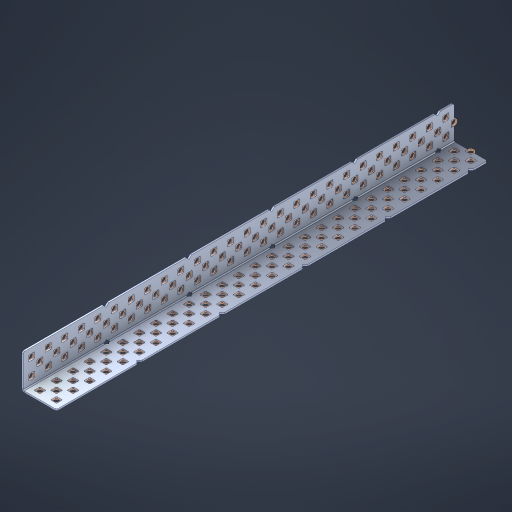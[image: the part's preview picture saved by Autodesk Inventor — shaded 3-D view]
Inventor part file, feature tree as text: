
AUTODESK INVENTOR PART (.ipt)
format: ipt  version: 2023 (Build 270158000, 158)  size: 1,872,384 bytes
history: native  units: in
note: dims shown in document units (in); Inventor stores cm internally (conversion verified against a paired STEP export)
features: other x162, extrude x154, sheet_metal_op x8, sketch x7, pattern_linear x2, mirror x1, chamfer x1
ambient origin geometry x8: Origin, YZ Plane, XZ Plane, XY Plane, X Axis, Y Axis, Z Axis, Center Point
bodies: Solid1 (feature_tree), Body (feature_tree)
feature tree (335):
  sheet_metal_op  "Flanges"
  sheet_metal_op  "Body Pattern"
  pattern_linear  "Center Pattern"  Spacing1=1.0in  [1 undecoded]
  other  "Arc Length"
  pattern_linear  "Notch Pattern"  Spacing1=0.1875in  [1 undecoded]
  other  "Diagonal Plane"
  mirror  "Everything Mirrored"
  chamfer  "End Chamfer"
  sketch  "Sketch1"  dims[d0=1.0in]
  other  "Plate1"
  sketch  "Sketch2"  dims[d1=13.0in]
  other  "Plate2"
  sheet_metal_op  "Bend1"
  sheet_metal_op  "Corner1"
  sketch  "Sketch8"  dims[d2=0.0469in]
  sketch  "Sketch9"  dims[d3=0.0469in]
  other  "Srf91"
  sheet_metal_op  "Body Pattern Sketch"
  other  "Srf92"
  sketch  "Sketch13"  dims[d4=0.0234in]
  sketch  "Sketch15"  dims[d5=0.0938in]
  sketch  "Sketch16"  dims[d6=0.0469in d7=1.0in d8=90.0deg d9=0.0312in d10=0.1875in d11=0.0469in d12=0.0469in d49=0.182in d50=0.02in d52=0.25in d53=0.0469in d54=0.0in d55=0.172in d56=1.0in d57=0.0in d60=10.2362in d62=0.5in d63=0.7874in d65=0.5in d85=0.1473in d86=0.1659in d89=0.0469in d90=0.0in d91=0.04in d92=0.0491in d95=2.5in d96=0.04in d97=0.25in d98=45.0deg d99=0.25in d106=0.182in d107=0.02in d108=0.5in d110=0.0469in d111=0.0in d112=0.172in d113=0.5in d114=0.0in d117=0.5in d123=0.25in d125=0.25in d126=0.0491in d127=0.1227in d128=0.08in d129=0.04in d130=2.5in]
  other  "Srf786"
  other  "Srf856"
  other  "Srf857"
  other  "Srf858"
  other  "Srf859"
  other  "Srf860"
  other  "Srf861"
  other  "Srf889"
  other  "Srf890"
  other  "Srf891"
  other  "Srf1275"
  other  "Srf1276"
  other  "Srf1278"
  other  "Srf1279"
  other  "Srf1280"
  other  "Srf1281"
  other  "Srf1282"
  other  "Srf1283"
  other  "Srf1277"
  other  "Srf1285"
  other  "Srf1286"
  other  "Srf1287"
  other  "Srf1383"
  other  "Srf1384"
  other  "Srf1385"
  other  "Srf1386"
  other  "Srf1387"
  other  "Srf1388"
  other  "Srf1389"
  other  "Srf1390"
  other  "Srf1391"
  other  "Srf1392"
  other  "Srf1393"
  other  "Srf1394"
  other  "Srf1395"
  other  "Srf1396"
  other  "Srf1397"
  other  "Srf1398"
  other  "Srf1399"
  other  "Srf1400"
  other  "Srf1401"
  other  "Srf1402"
  other  "Srf1403"
  other  "Srf1404"
  other  "Srf1405"
  other  "Srf1406"
  other  "Srf1407"
  other  "Srf1408"
  other  "Srf1409"
  other  "Srf1410"
  other  "Srf1411"
  other  "Srf1412"
  other  "Srf1413"
  other  "Srf1414"
  other  "Srf1415"
  other  "Srf1416"
  other  "Srf1417"
  other  "Srf1418"
  other  "Srf1419"
  other  "Srf1420"
  other  "Srf1421"
  other  "Srf1422"
  other  "Srf1423"
  other  "Srf1424"
  other  "Srf1425"
  other  "Srf1426"
  other  "Srf1445"
  other  "Srf1446"
  other  "Srf1447"
  other  "Srf1448"
  other  "Srf1449"
  other  "Srf1450"
  other  "Srf1451"
  other  "Srf1452"
  other  "Srf1453"
  other  "Srf1454"
  other  "Srf1455"
  other  "Srf1456"
  other  "Srf1457"
  other  "Srf1458"
  other  "Srf1459"
  other  "Srf1460"
  other  "Srf1461"
  other  "Srf1462"
  other  "Srf1463"
  other  "Srf1464"
  other  "Srf1465"
  other  "Srf1466"
  other  "Srf1475"
  other  "Srf1476"
  other  "Srf1477"
  other  "Srf1478"
  other  "Srf1479"
  other  "Srf1480"
  other  "Srf1481"
  other  "Srf1482"
  other  "Srf1483"
  other  "Srf1484"
  other  "Srf1485"
  other  "Srf1486"
  other  "Srf1487"
  other  "Srf1488"
  other  "Srf1489"
  other  "Srf1490"
  other  "Srf1491"
  other  "Srf1492"
  other  "Srf1493"
  other  "Srf1494"
  other  "Srf1495"
  other  "Srf1496"
  other  "Srf1497"
  other  "Srf1498"
  other  "Srf1499"
  other  "Srf1500"
  other  "Srf1501"
  other  "Srf1502"
  other  "Srf1503"
  other  "Srf1504"
  other  "Srf1505"
  other  "Srf1506"
  other  "Srf1507"
  other  "Srf1508"
  other  "Srf1509"
  other  "Srf1510"
  other  "Srf1511"
  other  "Srf1512"
  other  "Srf1513"
  other  "Srf1514"
  other  "Srf1515"
  other  "Srf1516"
  other  "Srf1517"
  other  "Srf1518"
  other  "Srf1537"
  other  "Srf1538"
  other  "Srf1539"
  other  "Srf1540"
  other  "Srf1541"
  other  "Srf1542"
  other  "Srf1543"
  other  "Srf1544"
  other  "Srf1545"
  other  "Srf1546"
  other  "Srf1547"
  other  "Srf1548"
  other  "Srf1549"
  other  "Srf1550"
  other  "Srf1551"
  other  "Srf1552"
  other  "Srf1553"
  other  "Srf1554"
  other  "Srf1555"
  other  "Srf1556"
  other  "Srf1557"
  other  "Srf1558"
  sheet_metal_op  "Body Stamp"
  sheet_metal_op  "Body Circle"
  other  "Center Stamp"
  other  "Center Circle"
  sheet_metal_op  "Notch"
  extrude  "ExtrusionSrf92"  Depth=0.0469in
  extrude  "ExtrusionSrf856"  Depth=0.0469in
  extrude  "ExtrusionSrf857"  Depth=0.182in
  extrude  "ExtrusionSrf858"  Depth=0.02in
  extrude  "ExtrusionSrf859"  Depth=0.25in
  extrude  "ExtrusionSrf860"  Depth=0.0469in
  extrude  "ExtrusionSrf861"  TaperAngle=0.0deg  [1 undecoded]
  extrude  "ExtrusionSrf889"  Depth=2.5in
  extrude  "ExtrusionSrf890"  Depth=1.0in TaperAngle=0.0deg
  extrude  "ExtrusionSrf891"  Depth=2.5in
  extrude  "ExtrusionSrf1275"  Depth=0.5in
  extrude  "ExtrusionSrf1276"  Depth=2.5in
  extrude  "ExtrusionSrf1277"  Depth=2.5in
  extrude  "ExtrusionSrf1278"  Depth=0.0469in
  extrude  "ExtrusionSrf1279"  Depth=2.5in TaperAngle=0.0deg
  extrude  "ExtrusionSrf1280"  Depth=2.5in
  extrude  "ExtrusionSrf1281"  Depth=0.25in TaperAngle=45.0deg
  extrude  "ExtrusionSrf1282"  Depth=0.25in
  extrude  "ExtrusionSrf1345"  Depth=0.182in
  extrude  "ExtrusionSrf1346"  Depth=0.02in
  extrude  "ExtrusionSrf1347"  Depth=0.5in
  extrude  "ExtrusionSrf1348"  Depth=0.0469in
  extrude  "ExtrusionSrf1383"  TaperAngle=0.0deg  [1 undecoded]
  extrude  "ExtrusionSrf1384"  Depth=2.5in
  extrude  "ExtrusionSrf1385"  Depth=0.5in TaperAngle=0.0deg
  extrude  "ExtrusionSrf1386"  Depth=0.5in
  extrude  "ExtrusionSrf1387"  Depth=0.25in
  extrude  "ExtrusionSrf1388"  Depth=0.25in
  extrude  "ExtrusionSrf1389"  Depth=2.5in
  extrude  "ExtrusionSrf1390"  Depth=2.5in
  extrude  "ExtrusionSrf1391"  Depth=2.5in
  extrude  "ExtrusionSrf1392"  Depth=2.5in
  extrude  "ExtrusionSrf1393"  Depth=2.5in
  extrude  "ExtrusionSrf1394"  [1 undecoded]
  extrude  "ExtrusionSrf1395"  [1 undecoded]
  extrude  "ExtrusionSrf1396"  [1 undecoded]
  extrude  "ExtrusionSrf1397"  [1 undecoded]
  extrude  "ExtrusionSrf1398"  [1 undecoded]
  extrude  "ExtrusionSrf1399"  [1 undecoded]
  extrude  "ExtrusionSrf1400"  [1 undecoded]
  extrude  "ExtrusionSrf1401"  [1 undecoded]
  extrude  "ExtrusionSrf1402"  [1 undecoded]
  extrude  "ExtrusionSrf1403"  [1 undecoded]
  extrude  "ExtrusionSrf1404"  [1 undecoded]
  extrude  "ExtrusionSrf1405"  [1 undecoded]
  extrude  "ExtrusionSrf1406"  [1 undecoded]
  extrude  "ExtrusionSrf1407"  [1 undecoded]
  extrude  "ExtrusionSrf1408"  [1 undecoded]
  extrude  "ExtrusionSrf1409"  [1 undecoded]
  extrude  "ExtrusionSrf1410"  [1 undecoded]
  extrude  "ExtrusionSrf1411"  [1 undecoded]
  extrude  "ExtrusionSrf1412"  [1 undecoded]
  extrude  "ExtrusionSrf1413"  [1 undecoded]
  extrude  "ExtrusionSrf1414"  [1 undecoded]
  extrude  "ExtrusionSrf1415"  [1 undecoded]
  extrude  "ExtrusionSrf1416"  [1 undecoded]
  extrude  "ExtrusionSrf1417"  [1 undecoded]
  extrude  "ExtrusionSrf1418"  [1 undecoded]
  extrude  "ExtrusionSrf1419"  [1 undecoded]
  extrude  "ExtrusionSrf1420"  [1 undecoded]
  extrude  "ExtrusionSrf1421"  [1 undecoded]
  extrude  "ExtrusionSrf1422"  [1 undecoded]
  extrude  "ExtrusionSrf1423"  [1 undecoded]
  extrude  "ExtrusionSrf1424"  [1 undecoded]
  extrude  "ExtrusionSrf1425"  [1 undecoded]
  extrude  "ExtrusionSrf1426"  [1 undecoded]
  extrude  "ExtrusionSrf1445"  [1 undecoded]
  extrude  "ExtrusionSrf1446"  [1 undecoded]
  extrude  "ExtrusionSrf1447"  [1 undecoded]
  extrude  "ExtrusionSrf1448"  [1 undecoded]
  extrude  "ExtrusionSrf1449"  [1 undecoded]
  extrude  "ExtrusionSrf1450"  [1 undecoded]
  extrude  "ExtrusionSrf1451"  [1 undecoded]
  extrude  "ExtrusionSrf1452"  [1 undecoded]
  extrude  "ExtrusionSrf1453"  [1 undecoded]
  extrude  "ExtrusionSrf1454"  [1 undecoded]
  extrude  "ExtrusionSrf1455"  [1 undecoded]
  extrude  "ExtrusionSrf1456"  [1 undecoded]
  extrude  "ExtrusionSrf1457"  [1 undecoded]
  extrude  "ExtrusionSrf1458"  [1 undecoded]
  extrude  "ExtrusionSrf1459"  [1 undecoded]
  extrude  "ExtrusionSrf1460"  [1 undecoded]
  extrude  "ExtrusionSrf1461"  [1 undecoded]
  extrude  "ExtrusionSrf1462"  [1 undecoded]
  extrude  "ExtrusionSrf1463"  [1 undecoded]
  extrude  "ExtrusionSrf1464"  [1 undecoded]
  extrude  "ExtrusionSrf1465"  [1 undecoded]
  extrude  "ExtrusionSrf1466"  [1 undecoded]
  extrude  "ExtrusionSrf1475"  [1 undecoded]
  extrude  "ExtrusionSrf1476"  [1 undecoded]
  extrude  "ExtrusionSrf1477"  [1 undecoded]
  extrude  "ExtrusionSrf1478"  [1 undecoded]
  extrude  "ExtrusionSrf1479"  [1 undecoded]
  extrude  "ExtrusionSrf1480"  [1 undecoded]
  extrude  "ExtrusionSrf1481"  [1 undecoded]
  extrude  "ExtrusionSrf1482"  [1 undecoded]
  extrude  "ExtrusionSrf1483"  [1 undecoded]
  extrude  "ExtrusionSrf1484"  [1 undecoded]
  extrude  "ExtrusionSrf1485"  [1 undecoded]
  extrude  "ExtrusionSrf1486"  [1 undecoded]
  extrude  "ExtrusionSrf1487"  [1 undecoded]
  extrude  "ExtrusionSrf1488"  [1 undecoded]
  extrude  "ExtrusionSrf1489"  [1 undecoded]
  extrude  "ExtrusionSrf1490"  [1 undecoded]
  extrude  "ExtrusionSrf1491"  [1 undecoded]
  extrude  "ExtrusionSrf1492"  [1 undecoded]
  extrude  "ExtrusionSrf1493"  [1 undecoded]
  extrude  "ExtrusionSrf1494"  [1 undecoded]
  extrude  "ExtrusionSrf1495"  [1 undecoded]
  extrude  "ExtrusionSrf1496"  [1 undecoded]
  extrude  "ExtrusionSrf1497"  [1 undecoded]
  extrude  "ExtrusionSrf1498"  [1 undecoded]
  extrude  "ExtrusionSrf1499"  [1 undecoded]
  extrude  "ExtrusionSrf1500"  [1 undecoded]
  extrude  "ExtrusionSrf1501"  [1 undecoded]
  extrude  "ExtrusionSrf1502"  [1 undecoded]
  extrude  "ExtrusionSrf1503"  [1 undecoded]
  extrude  "ExtrusionSrf1504"  [1 undecoded]
  extrude  "ExtrusionSrf1505"  [1 undecoded]
  extrude  "ExtrusionSrf1506"  [1 undecoded]
  extrude  "ExtrusionSrf1507"  [1 undecoded]
  extrude  "ExtrusionSrf1508"  [1 undecoded]
  extrude  "ExtrusionSrf1509"  [1 undecoded]
  extrude  "ExtrusionSrf1510"  [1 undecoded]
  extrude  "ExtrusionSrf1511"  [1 undecoded]
  extrude  "ExtrusionSrf1512"  [1 undecoded]
  extrude  "ExtrusionSrf1513"  [1 undecoded]
  extrude  "ExtrusionSrf1514"  [1 undecoded]
  extrude  "ExtrusionSrf1515"  [1 undecoded]
  extrude  "ExtrusionSrf1516"  [1 undecoded]
  extrude  "ExtrusionSrf1517"  [1 undecoded]
  extrude  "ExtrusionSrf1518"  [1 undecoded]
  extrude  "ExtrusionSrf1537"  [1 undecoded]
  extrude  "ExtrusionSrf1538"  [1 undecoded]
  extrude  "ExtrusionSrf1539"  [1 undecoded]
  extrude  "ExtrusionSrf1540"  [1 undecoded]
  extrude  "ExtrusionSrf1541"  [1 undecoded]
  extrude  "ExtrusionSrf1542"  [1 undecoded]
  extrude  "ExtrusionSrf1543"  [1 undecoded]
  extrude  "ExtrusionSrf1544"  [1 undecoded]
  extrude  "ExtrusionSrf1545"  [1 undecoded]
  extrude  "ExtrusionSrf1546"  [1 undecoded]
  extrude  "ExtrusionSrf1547"  [1 undecoded]
  extrude  "ExtrusionSrf1548"  [1 undecoded]
  extrude  "ExtrusionSrf1549"  [1 undecoded]
  extrude  "ExtrusionSrf1550"  [1 undecoded]
  extrude  "ExtrusionSrf1551"  [1 undecoded]
  extrude  "ExtrusionSrf1552"  [1 undecoded]
  extrude  "ExtrusionSrf1553"  [1 undecoded]
  extrude  "ExtrusionSrf1554"  [1 undecoded]
  extrude  "ExtrusionSrf1555"  [1 undecoded]
  extrude  "ExtrusionSrf1556"  [1 undecoded]
  extrude  "ExtrusionSrf1557"  [1 undecoded]
  extrude  "ExtrusionSrf1558"  [1 undecoded]
note: 125 required parameter values undecoded (feature->parameter linkage not recoverable at this tier; creation-order binding heuristic only, values carry confidence <= 0.55)
